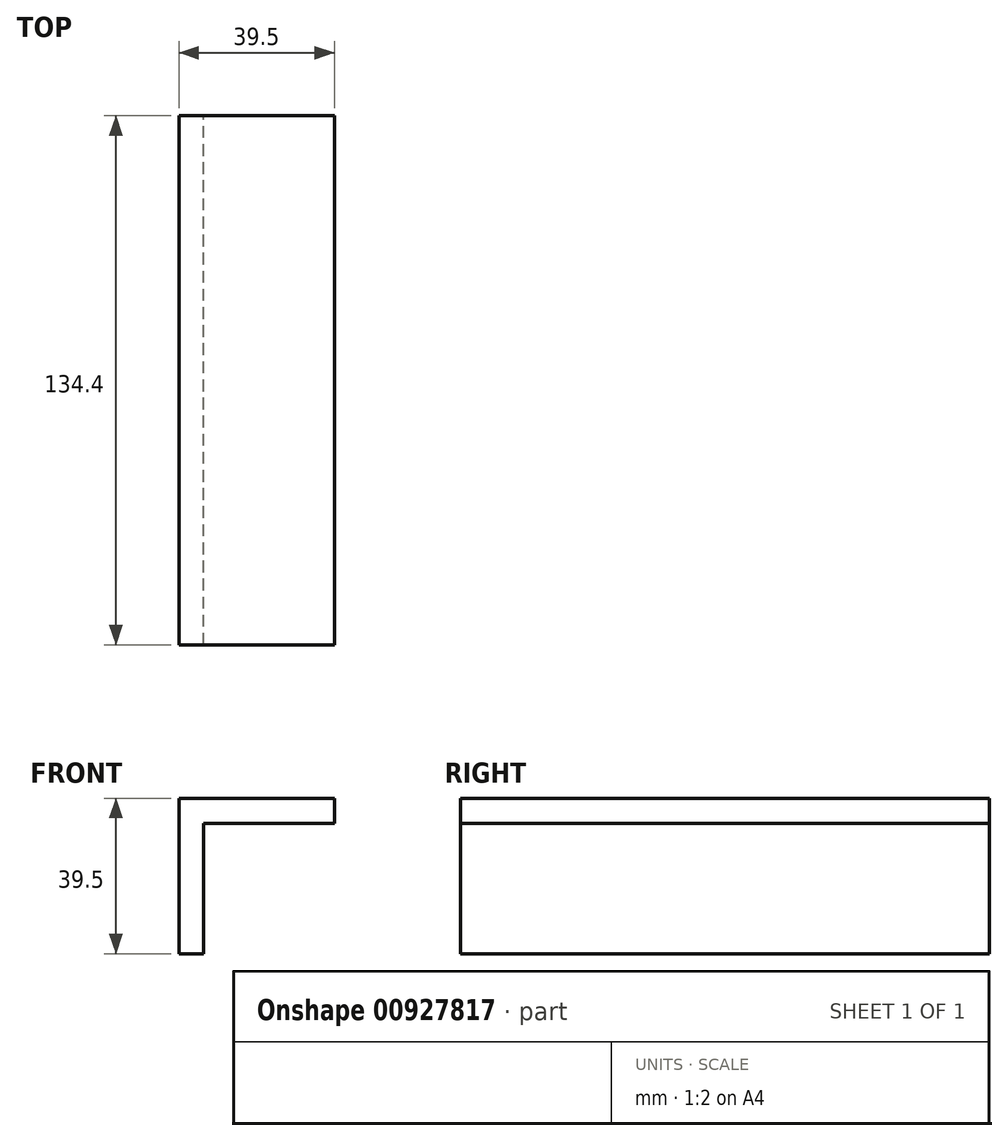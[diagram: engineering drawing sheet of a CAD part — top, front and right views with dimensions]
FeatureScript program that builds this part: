
annotation { "Feature Type Name" : "Feature", "Feature Type Description" : "" }
export const myFeature = defineFeature(function(context is Context, id is Id, definition is map)
    precondition{}
    {
        {
            var Q0;
            Q0=qCreatedBy(makeId("Front.planeOp"),FACE);
            var sketch = newSketch(context, id + "F0", { "sketchPlane" : qUnion([Q0])});
            skLineSegment(sketch, "E0", {"start": v(0.08, 0) * mm, "end": v(0.08, 39.5) * mm});
            skLineSegment(sketch, "E1", {"start": v(0.08, 39.5) * mm, "end": v(39.58, 39.5) * mm});
            skLineSegment(sketch, "E2", {"start": v(39.58, 39.5) * mm, "end": v(39.58, 33.15) * mm});
            skLineSegment(sketch, "E3", {"start": v(39.58, 33.15) * mm, "end": v(6.35, 33.15) * mm});
            skLineSegment(sketch, "E4", {"start": v(6.35, 33.15) * mm, "end": v(6.35, 0) * mm});
            skLineSegment(sketch, "E5", {"start": v(6.35, 0) * mm, "end": v(0, 0) * mm});
            skSolve(sketch);
        }
        {
            var Q0;
            Q0=qSketchRegion(id+"F0",true);
            extrude(context, id + "F1", {"entities" : qUnion([Q0]), "depth" : 134.4 * mm, "offsetDistance" : 25 * mm});
        }
    });
